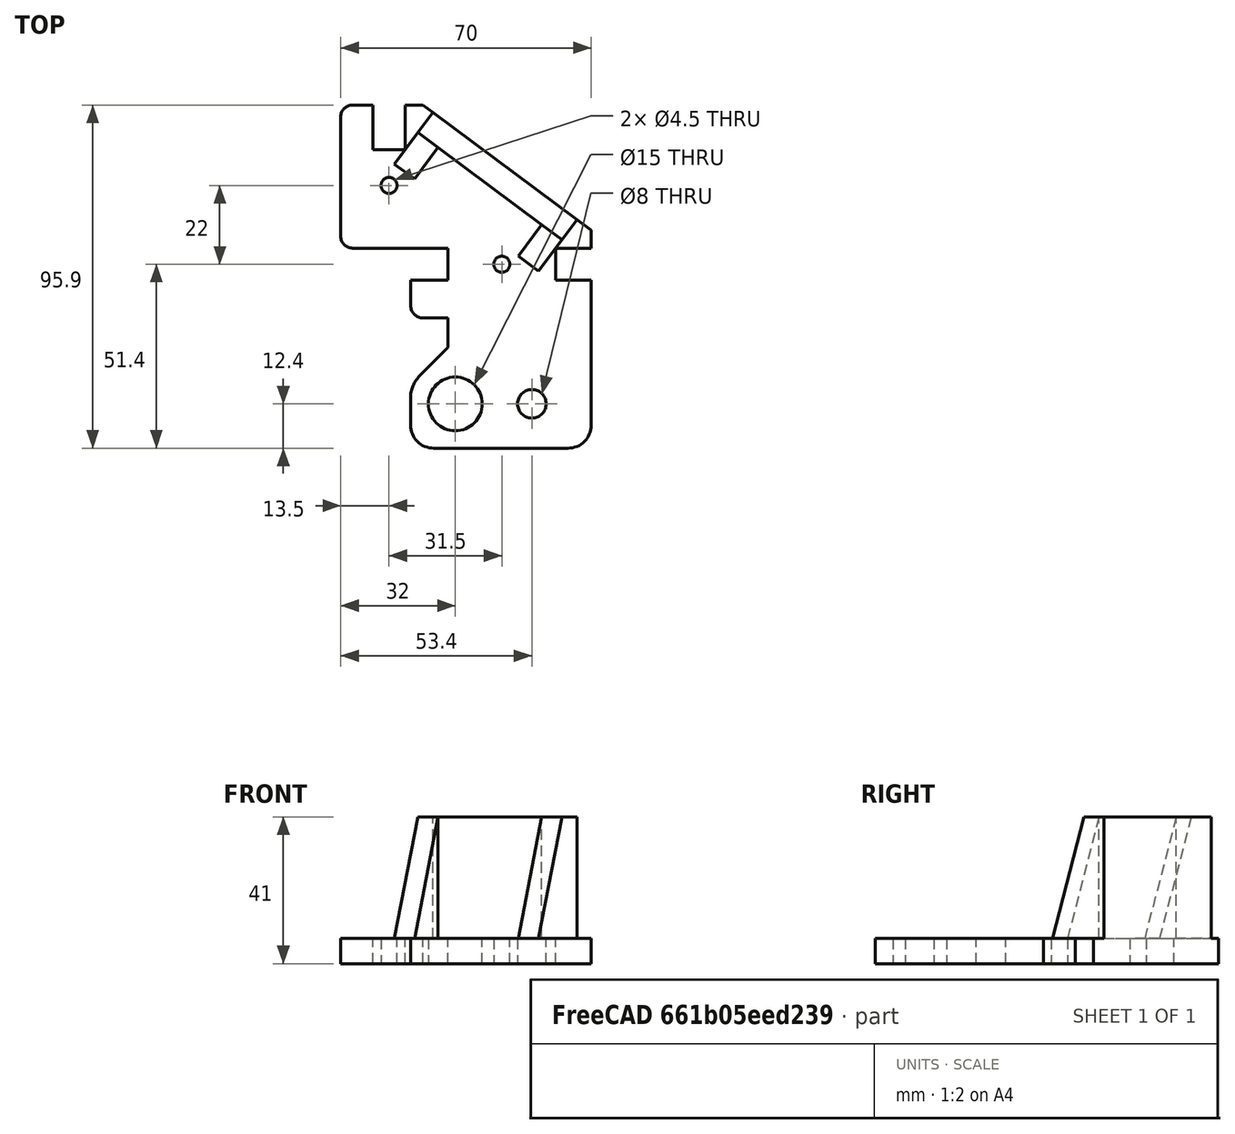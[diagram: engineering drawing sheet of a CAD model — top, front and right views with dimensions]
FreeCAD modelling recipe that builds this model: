
FCSTD DOCUMENT  (FreeCAD 1.0R39319 (Git))
Label: Bowden Extruder Mount
License: Creative Commons Attribution 4.0
LicenseURL: https://creativecommons.org/licenses/by/4.0/
objects: Sketcher::SketchObject×4, PartDesign::Pad×4, Mesh::Feature×1, Part::Feature×1, PartDesign::Body×1
note: 22 computed .brp shape members not serialized (recipe doc carries the construction recipe); baked Part::Feature solids carry a one-line shape summary decoded from their .brp

FEATURE [Mesh::Feature] BOWDEN_EXTRUDER_TOP_PLATE_RHS
FEATURE [Part::Feature] BOWDEN_EXTRUDER_TOP_PLATE_RHS001
  Placement = pos=(25,51.4,0) rot=(0,0,1;0rad)
  shape: bbox 74.53 x 103.5 x 41 mm, 3568 faces, 0 solids (baked)
FEATURE [Sketcher::SketchObject] Sketch
  ArcFitTolerance = 1e-06
  AttachmentSupport = -> [XY_Plane]
  FullyConstrained = true
  MakeInternals = false
  MapMode = 5
  sketch-geometry (41):
    g0: LineSegment StartX=3.3 StartY=95.9 StartZ=0 EndX=9 EndY=95.9 EndZ=0
    g1: LineSegment StartX=9 StartY=95.9 StartZ=0 EndX=9 EndY=83.4 EndZ=0
    g2: LineSegment StartX=9 StartY=83.4 StartZ=0 EndX=18 EndY=83.4 EndZ=0
    g3: LineSegment StartX=18 StartY=83.4 StartZ=0 EndX=18 EndY=95.9 EndZ=0
    g4: LineSegment StartX=23 StartY=95.9 StartZ=0 EndX=70 EndY=60.9 EndZ=0
    g5: LineSegment StartX=70 StartY=60.9 StartZ=0 EndX=70 EndY=55.9 EndZ=0
    g6: LineSegment StartX=70 StartY=55.9 StartZ=0 EndX=60 EndY=55.9 EndZ=0
    g7: LineSegment StartX=60 StartY=55.9 StartZ=0 EndX=60 EndY=46.9 EndZ=0
    g8: LineSegment StartX=60 StartY=46.9 StartZ=0 EndX=70 EndY=46.9 EndZ=0
    g9: LineSegment StartX=70 StartY=46.9 StartZ=0 EndX=70 EndY=6.5 EndZ=0
    g10: LineSegment StartX=63.5 StartY=0 StartZ=0 EndX=26 EndY=0 EndZ=0
    g11: LineSegment StartX=19.5 StartY=6.5 StartZ=0 EndX=19.5 EndY=13.9721 EndZ=0
    g12: LineSegment StartX=22.136 StartY=20.336 StartZ=0 EndX=30 EndY=28.2 EndZ=0
    g13: LineSegment StartX=30 StartY=28.2 StartZ=0 EndX=30 EndY=36.4 EndZ=0
    g14: LineSegment StartX=30 StartY=36.4 StartZ=0 EndX=23 EndY=36.4 EndZ=0
    g15: LineSegment StartX=19.55 StartY=39.85 StartZ=0 EndX=19.55 EndY=46.9 EndZ=0
    g16: LineSegment StartX=19.55 StartY=46.9 StartZ=0 EndX=30 EndY=46.9 EndZ=0
    g17: LineSegment StartX=30 StartY=46.9 StartZ=0 EndX=30 EndY=55.9 EndZ=0
    g18: LineSegment StartX=30 StartY=55.9 StartZ=0 EndX=3.3 EndY=55.9 EndZ=0
    g19: LineSegment StartX=0 StartY=59.2 StartZ=0 EndX=0 EndY=92.6 EndZ=0
    g20: ArcOfCircle CenterX=63.5 CenterY=6.5 CenterZ=0 NormalX=0 NormalY=0 NormalZ=1 AngleXU=0 Radius=6.5 StartAngle=4.71239 EndAngle=6.28319
    g21: GeomPoint [constr] X=70 Y=0 Z=0
    g22: ArcOfCircle CenterX=26 CenterY=6.5 CenterZ=0 NormalX=0 NormalY=0 NormalZ=1 AngleXU=0 Radius=6.5 StartAngle=3.14159 EndAngle=4.71239
    g23: GeomPoint [constr] X=19.5 Y=0 Z=0
    g24: ArcOfCircle CenterX=28.5 CenterY=13.9721 CenterZ=0 NormalX=0 NormalY=0 NormalZ=1 AngleXU=0 Radius=9 StartAngle=2.35619 EndAngle=3.14159
    g25: GeomPoint [constr] X=19.5 Y=17.7 Z=0
    g26: ArcOfCircle CenterX=3.3 CenterY=92.6 CenterZ=0 NormalX=0 NormalY=0 NormalZ=1 AngleXU=0 Radius=3.3 StartAngle=1.5708 EndAngle=3.14159
    g27: GeomPoint [constr] X=0 Y=95.9 Z=0
    g28: ArcOfCircle CenterX=3.3 CenterY=59.2 CenterZ=0 NormalX=0 NormalY=0 NormalZ=1 AngleXU=0 Radius=3.3 StartAngle=3.14159 EndAngle=4.71239
    g29: GeomPoint [constr] X=0 Y=55.9 Z=0
    g30: ArcOfCircle CenterX=23 CenterY=39.85 CenterZ=0 NormalX=0 NormalY=0 NormalZ=1 AngleXU=0 Radius=3.45 StartAngle=3.14159 EndAngle=4.71239
    g31: GeomPoint [constr] X=19.55 Y=36.4 Z=0
    g32: LineSegment StartX=23 StartY=95.9 StartZ=0 EndX=18 EndY=95.9 EndZ=0
    g33: GeomPoint X=60 Y=51.4 Z=0
    g34: GeomPoint X=30 Y=51.4 Z=0
    g35: GeomPoint X=45 Y=51.4 Z=0
    g36: Circle CenterX=45 CenterY=51.4 CenterZ=0 NormalX=0 NormalY=0 NormalZ=1 AngleXU=0 Radius=2.25
    g37: Circle CenterX=13.5 CenterY=73.4 CenterZ=0 NormalX=0 NormalY=0 NormalZ=1 AngleXU=0 Radius=2.25
    g38: GeomPoint X=13.5 Y=83.4 Z=0
    g39: Circle CenterX=53.4 CenterY=12.4 CenterZ=0 NormalX=0 NormalY=0 NormalZ=1 AngleXU=0 Radius=4
    g40: Circle CenterX=32 CenterY=12.4 CenterZ=0 NormalX=0 NormalY=0 NormalZ=1 AngleXU=0 Radius=7.5
  constraints (102):
    c: PointOnObject(g27,g-2)
    c: Horizontal(g0)
    c: Coincident(g0,g1)
    c: Vertical(g1)
    c: Coincident(g1,g2)
    c: Coincident(g2,g3)
    c: Vertical(g3)
    c: Coincident(g4,g5)
    c: Vertical(g5)
    c: Coincident(g5,g6)
    c: Coincident(g6,g7)
    c: Coincident(g7,g8)
    c: Coincident(g8,g9)
    c: PointOnObject(g21,g-1)
    c: Vertical(g9)
    c: PointOnObject(g23,g-1)
    c: Coincident(g12,g13)
    c: Vertical(g13)
    c: Coincident(g13,g14)
    c: Horizontal(g14)
    c: Vertical(g15)
    c: Coincident(g15,g16)
    c: Coincident(g16,g17)
    c: Vertical(g17)
    c: Coincident(g17,g18)
    c: PointOnObject(g29,g-2)
    c: Horizontal(g6)
    c: Horizontal(g8)
    c: Horizontal(g16)
    c: Horizontal(g18)
    c: Horizontal(g2)
    c: Vertical(g7)
    c: Vertical(g11)
    c: PointOnObject(g21,g9)
    c: PointOnObject(g21,g10)
    c: Tangent(g9,g20) = 1.5708
    c: Tangent(g10,g20) = 1.5708
    c: PointOnObject(g23,g10)
    c: PointOnObject(g23,g11)
    c: Tangent(g10,g22) = 1.5708
    c: Tangent(g11,g22) = 1.5708
    c: PointOnObject(g25,g11)
    c: PointOnObject(g25,g12)
    c: Tangent(g11,g24) = 1.5708
    c: Tangent(g12,g24) = 1.5708
    c: PointOnObject(g27,g0)
    c: PointOnObject(g27,g19)
    c: Tangent(g0,g26) = 1.5708
    c: Tangent(g19,g26) = 1.5708
    c: PointOnObject(g29,g18)
    c: PointOnObject(g29,g19)
    c: Tangent(g18,g28) = 1.5708
    c: Tangent(g19,g28) = 1.5708
    c: DistanceX(g11) = 19.5
    c: Radius(g22) = 6.5
    c: Angle(g11,g12) = 2.35619
    c: Radius(g24) = 9
    c: DistanceX(g12) = 30
    c: DistanceY(g12) = 28.2
    c: PointOnObject(g31,g14)
    c: PointOnObject(g31,g15)
    c: Tangent(g14,g30) = 1.5708
    c: Tangent(g15,g30) = 1.5708
    c: DistanceY(g13,g13) = 8.2
    c: DistanceX(g15) = 19.55
    c: Radius(g30) = 3.45
    c: DistanceY(g14,g15) = 10.5
    c: Vertical(g13,g16)
    c: DistanceY(g17,g17) = 9
    c: Radius(g28) = 3.3
    c: DistanceY(g0) = 95.9
    c: Equal(g28,g26)
    c: DistanceY(g1,g1) = 12.5
    c: Equal(g7,g2)
    c: Horizontal(g3,g0)
    c: Equal(g17,g2)
    c: DistanceX(g0) = 9
    c: DistanceX(g11,g9) = 50.5
    c: Equal(g22,g20)
    c: Horizontal(g7,g16)
    c: DistanceX(g8,g8) = 10
    c: Vertical(g8,g5)
    c: DistanceY(g5,g5) = 5
    c: Coincident(g32,g4)
    c: Horizontal(g32)
    c: DistanceX(g32,g32) = 5
    c: Coincident(g32,g3)
    c: Symmetric(g7,g7,g33)
    c: Symmetric(g17,g17,g34)
    c: Symmetric(g33,g34,g35)
    c: Coincident(g36,g35)
    c: Diameter(g36) = 4.5
    c: Symmetric(g2,g2,g38)
    c: Vertical(g37,g38)
    c: Equal(g37,g36)
    c: DistanceY(g17,g37) = 17.5
    c: Horizontal(g39,g40)
    c: Diameter(g40) = 15
    c: DistanceX(g40,g35) = 13
    c: DistanceY(g40,g35) = 39
    c: Diameter(g39) = 8
    c: DistanceX(g40,g39) = 21.4
FEATURE [PartDesign::Pad] Pad
  Direction = (0,0,1)
  Length = 7
  Length2 = 10
  Profile = -> Sketch
  ReferenceAxis = -> Sketch [N_Axis]
  Refine = true
  Suppressed = false
  Type = 0
FEATURE [Sketcher::SketchObject] Sketch001
  ArcFitTolerance = 1e-06
  AttachmentSupport = -> [Pad]
  ExternalGeometry = -> [Pad]
  FullyConstrained = true
  MakeInternals = false
  MapMode = 5
  Placement = pos=(0,0,7) rot=(0,0,1;0rad)
  expr: Constraints[9] = <<Pad>>.Length
  sketch-geometry (4):
    g0: LineSegment StartX=25.7715 StartY=93.8361 StartZ=0 EndX=65.9624 EndY=63.9067 EndZ=0
    g1: LineSegment StartX=65.9624 StartY=63.9067 StartZ=0 EndX=61.7816 EndY=58.2924 EndZ=0
    g2: LineSegment StartX=61.7816 StartY=58.2924 StartZ=0 EndX=21.5907 EndY=88.2218 EndZ=0
    g3: LineSegment StartX=21.5907 StartY=88.2218 StartZ=0 EndX=25.7715 EndY=93.8361 EndZ=0
  constraints (13):
    c: PointOnObject(g0,g-5)
    c: PointOnObject(g0,g-5)
    c: Coincident(g0,g1)
    c: Coincident(g1,g2)
    c: Coincident(g2,g3)
    c: Coincident(g3,g0)
    c: Perpendicular(g1,g0)
    c: Perpendicular(g3,g2)
    c: Equal(g2,g0)
    c: Distance(g1) = 7
    c: PointOnObject(g-3,g1)
    c: PointOnObject(g-4,g3)
    c: Distance(g0) = 50.1106
FEATURE [PartDesign::Pad] Pad001
  BaseFeature = -> Pad
  Direction = (0,0,1)
  Length = 34
  Length2 = 10
  Profile = -> Sketch001
  ReferenceAxis = -> Sketch001 [N_Axis]
  Refine = true
  Suppressed = false
  Type = 0
FEATURE [Sketcher::SketchObject] Sketch002
  ArcFitTolerance = 1e-06
  AttachmentSupport = -> [Pad001]
  ExternalGeometry = -> [Pad001]
  FullyConstrained = true
  MakeInternals = false
  MapMode = 5
  Placement = pos=(11.8184,-8.80096,0) rot=(0.815334,0.409408,0.409408;1.77355rad)
  sketch-geometry (3):
    g0: LineSegment StartX=83.6531 StartY=41 StartZ=0 EndX=72.6531 EndY=7 EndZ=0
    g1: LineSegment StartX=72.6531 StartY=7 StartZ=0 EndX=83.6531 EndY=7 EndZ=0
    g2: LineSegment StartX=83.6531 StartY=7 StartZ=0 EndX=83.6531 EndY=41 EndZ=0
  constraints (7):
    c: Coincident(g-3,g0)
    c: Coincident(g0,g1)
    c: Coincident(g1,g-3)
    c: Horizontal(g1)
    c: Coincident(g1,g2)
    c: Coincident(g2,g0)
    c: DistanceX(g1,g1) = 11
FEATURE [PartDesign::Pad] Pad002
  BaseFeature = -> Pad001
  Direction = (0.802043,-0.597266,-1e-16)
  Length = 7
  Length2 = 10
  Profile = -> Sketch002
  ReferenceAxis = -> Sketch002 [N_Axis]
  Refine = true
  Reversed = true
  Suppressed = false
  Type = 0
  expr: Length = <<Pad>>.Length
FEATURE [Sketcher::SketchObject] Sketch003
  ArcFitTolerance = 1e-06
  AttachmentSupport = -> [Pad002]
  ExternalGeometry = -> [Pad002]
  FullyConstrained = true
  MakeInternals = false
  MapMode = 5
  Placement = pos=(-28.3725,21.1284,0) rot=(-0.334598,0.66635,0.66635;3.78737rad)
  sketch-geometry (3):
    g0: LineSegment StartX=-72.6531 StartY=7 StartZ=0 EndX=-83.6531 EndY=7 EndZ=0
    g1: LineSegment StartX=-83.6531 StartY=7 StartZ=0 EndX=-83.6531 EndY=41 EndZ=0
    g2: LineSegment StartX=-83.6531 StartY=41 StartZ=0 EndX=-72.6531 EndY=7 EndZ=0
  constraints (7):
    c: Coincident(g-3,g0)
    c: Coincident(g0,g1)
    c: Coincident(g1,g-3)
    c: Vertical(g1)
    c: Coincident(g1,g2)
    c: Coincident(g2,g0)
    c: Horizontal(g0)
FEATURE [PartDesign::Pad] Pad003
  BaseFeature = -> Pad002
  Direction = (-0.802043,0.597266,-1e-16)
  Length = 7
  Length2 = 10
  Profile = -> Sketch003
  ReferenceAxis = -> Sketch003 [N_Axis]
  Refine = true
  Reversed = true
  Suppressed = false
  Type = 0
  expr: Length = Pad.Length
FEATURE [PartDesign::Body] Body  label="Bowden Extruder Mount"
  AllowCompound = false
  Group = -> [Sketch,Pad,Sketch001,Pad001,Sketch002,Pad002,Sketch003,Pad003]
  Origin = -> Origin
  Tip = -> Pad003
